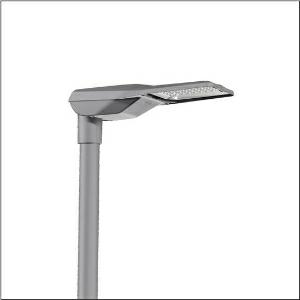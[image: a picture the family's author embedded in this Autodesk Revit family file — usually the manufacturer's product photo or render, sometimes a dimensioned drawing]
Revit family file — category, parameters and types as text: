
# Revit family: streetlight_sl_21_iq_mini___p1_0a_5xe2a31d08gb_969e
name_source: partatom
category: Lighting Fixtures
units: mm (PartAtom-declared; Revit-internal decimal feet)

## family parameters
Cut with Voids When Loaded = No
Host = Face
Light Source = No
Part Type = Normal
Room Calculation Point = No
Round Connector Dimension = Use Diameter
Shared = No

## types (1)
- --- (1 x LED, 5680 lm, 37.1 W, 3000K)
    Apparent Load = 37 VA
    CIE Flux Codes = 21 50 90 100 100
    Color Rendering = 70
    Color Temperature = 3000K
    Default Elevation = 1800 mm
    Description = Streetlight SL 21 iQ mini, mast luminaire, primary light control with lens, of PMMA, primary optical cover: cover, of toughened safety glass, transparent, light distribution: P1.0a, light emission: direct distribution, primary light characteristic: asymmetric, installation type: post-top, side-entry, LED, High Power LED, rated luminous flux: 5.680lm, luminous efficacy: 153lm/W, light colour: 730, colour temperature: 3000K, control gear: iQ-Comfort, control: Auto-Match, Temp-Guard, Lumen-Switch, Night-Set, Smart-Wire, Light-Fading, Desk-Remote (wireless, voltage-free reading and setting of iQ features in the workshop via application-optimized NFC function/RFID function), optimised constant luminous flux control (CLO 2.0), pre-setting: linear dimming characteristic, mains connection: 220..240V, AC, 50/60Hz, start of lifetime: 37W, end of service life: 39W, reduction: 18W, luminaire housing, of diecast aluminium, powder-coated, SITECO metallic grey (DB 702S), corrosivity category C5 high according to DIN EN ISO 12944, please order mast flange separately, inclination adjustable: 0°, 5°, 10°, 15°, sealing non-destructively replaceable, multi-level sealing system, length: 628mm, width: 235mm, height: 110mm, mast flange for spigot size: 42mm (side-entry): 5XC10008XM4, 60/48mm (side-entry/post-top): 5XC10108XM2, 76/60mm (side-entry/post-top): 5XC10108XM1, mounting height: 4..8m, protection rating (complete): IP66, insulation class (complete): insulation class II (safety insulation), certification: CE, ENEC, ENEC+, VDE, impact resistance: IK10, permissible operating ambient temperature for outdoor applications: -40..+50°C, standard-compliant lighting for roads and squares, packaging unit: 1 piece

Light Distribution: P1.0a
    Height = 110 mm
    Lamp = 1 x LED
    Lamp Light Flux = 5680 lm
    Lamp Power = 37.1 W
    Lamp count = 1
    Length = 625 mm
    Luminous efficacy = 153 lm/W
    Manufacturer = Siteco
    ModVariant = No
    Model = 5XE2A31D08GB
    Number of Poles = 1
    OnlyDefault = Yes
    Power Factor = 1
    Product Name = Streetlight SL 21 iQ mini | P1.0a
    Product group = mast luminaire | pylon top
    ProductGroupID = 6100
    Protection Class = Protection class II
    Protection Degree = IP 66
    RLX_Detail_Level = 1
    RLX_Emergency_Light_Flux = 0 lm
    RLX_Emergency_Type = 0
    RLX_Emergency_Type_DB = No
    RlxData = <blob elided: 37617 chars, md5=4b585fd4>
    Socket = socket
    Standby Power = 0 W
    System Light Flux = 5680 lm
    System Power = 37 W
    Type Comments = factory setting: luminous flux: 100 % | dim-lin: 254 | 385 mA
    Type Image = l_1003519.jpg
    URL = http://relux.com
    VarID = @adj_184317
    Voltage = 0 V
    Weight = 0.00 kg
    Width = 234 mm

## geometry (parser evidence)
native form markers: Blend x4, Sweep x9
no freeform markers — native parametric forms only
